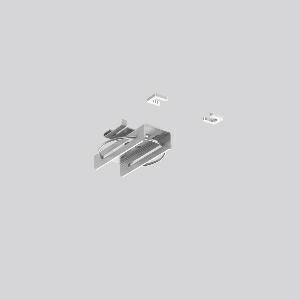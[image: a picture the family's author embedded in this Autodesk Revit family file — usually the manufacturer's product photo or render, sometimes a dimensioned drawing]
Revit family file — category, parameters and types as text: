
# Revit family: linedo_decke_adapter_caddyclip_982666_000_5787
name_source: partatom
category: Lighting Fixtures
units: mm (PartAtom-declared; Revit-internal decimal feet)

## family parameters
Cut with Voids When Loaded = No
Host = Face
Light Source = No
Part Type = Normal
Room Calculation Point = No
Round Connector Dimension = Use Diameter
Shared = No

## types (1)
- LINEDO Decke Adapter Caddyclip
    Apparent Load = 0 VA
    Default Elevation = 1800 mm
    Description = Series: LINEDO
Adapter for direct ceiling installation in grid ceilings (caddy clip). Galvanised sheet steel, for installing continuous line luminaire modules. Incl. 2 locking brackets.
Colour: unpainted
Length: 70 mm
Width: 54 mm
Height: 22 mm
Weight: 25 g
Type of Installation: Ceiling mounting
    Height = 22 mm
    Lamp = 0 x
    Length = 70 mm
    Luminous efficacy = 0 lm/W
    Manufacturer = RZB
    ModVariant = No
    Model = 982666.000
    Mounting Place = Ceiling
    Mounting Type = Surface mounted
    Number of Poles = 1
    OnlyDefault = Yes
    Power Factor = 1
    Product Name = LINEDO Decke Adapter Caddyclip
    Product group = Surface mounted continuous line luminaire system
    ProductGroupID = 310
    Protection Class = Protection class
    Protection Degree = Degree of protection
    RLX_Detail_Level = 1
    RLX_Emergency_Light_Flux = 0 lm
    RLX_Emergency_Type = 0
    RLX_Emergency_Type_DB = No
    RlxData = <blob elided: 9853 chars, md5=08b24874>
    Standby Power = 0 W
    System Light Flux = 0 lm
    System Power = 0 W
    Type Comments = Product without accessories
    Type Image = 982666.000.jpg
    URL = http://relux.com
    VarID = ---
    Voltage = 0 V
    Weight = 0.00 kg
    Width = 54 mm

## geometry (parser evidence)
native form markers: Sweep x9
no freeform markers — native parametric forms only
